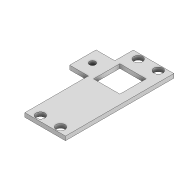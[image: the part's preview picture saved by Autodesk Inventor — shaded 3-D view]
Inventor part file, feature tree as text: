
AUTODESK INVENTOR PART (.ipt)
format: ipt  version: 2021 (Build 250183000, 183)  size: 112,640 bytes
history: native  units: mm
features: other x1, extrude x1, sketch x1
ambient origin geometry x8: Origin, YZ Plane, XZ Plane, XY Plane, X Axis, Y Axis, Z Axis, Center Point
bodies: Body1 (feature_tree)
feature tree (3):
  other  "Sólido1"
  extrude  "Extrusión1"  TaperAngle=90.0deg  [1 undecoded]
  sketch  "Boceto1"  dims[d8=53.4mm d9=90.0deg d10=20.0mm d11=2.6mm d12=4.95mm d13=9.9mm d14=4.4mm d15=4.4mm d16=2.6mm d19=4.4mm d20=4.4mm d26=13.5mm d27=3.0mm d28=2.0mm d29=0.0mm]
note: 1 required parameter value undecoded (feature->parameter linkage not recoverable at this tier; creation-order binding heuristic only, values carry confidence <= 0.55)
